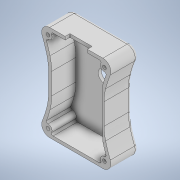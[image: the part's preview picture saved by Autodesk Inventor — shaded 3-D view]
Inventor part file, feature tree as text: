
AUTODESK INVENTOR PART (.ipt)
format: ipt  version: 2021 (Build 250183000, 183)  size: 397,824 bytes
history: native  units: mm
features: extrude x8, sketch x8, mirror x6, fillet x6, shell x2, projected_geometry x2
ambient origin geometry x8: Origin, YZ Plane, XZ Plane, XY Plane, X Axis, Y Axis, Z Axis, Center Point
bodies: Solid1 (feature_tree)
feature tree (32):
  extrude  "Extrusion1"  Depth=17.25mm
  shell  "Shell1"  Thickness=17.25mm
  extrude  "Extrusion2"  Depth=2.0mm
  mirror  "Mirror1"
  mirror  "Mirror2"
  fillet  "Fillet2"  Radius=20.0mm
  fillet  "Fillet3"  Radius=75.0mm
  shell  "Shell2"  Thickness=16.75mm
  extrude  "Extrusion3"  Depth=30.0mm
  mirror  "Mirror3"
  mirror  "Mirror4"
  fillet  "Fillet4"  Radius=5.0mm
  extrude  "Extrusion4"  Depth=2.0mm
  extrude  "Extrusion5"  Depth=5.0mm
  mirror  "Mirror5"
  mirror  "Mirror6"
  fillet  "Fillet5"  Radius=1.0mm
  extrude  "Extrusion6"  Depth=10.0mm
  extrude  "Extrusion8"  Depth=3.75mm
  fillet  "Fillet6"  Radius=8.0mm
  extrude  "Extrusion10"  Depth=0.5mm
  fillet  "Fillet7"  Radius=2.54mm
  sketch  "Sketch1"  dims[d0=35.0mm d1=60.0mm d2=17.25mm d3=0.0mm]
  sketch  "Sketch2"  dims[d4=2.0mm d5=7.0mm d7=20.0mm d8=75.0mm d9=16.75mm d10=0.0mm]
  sketch  "Sketch3"  dims[d12=2.0mm d13=30.0mm d14=5.0mm]
  sketch  "Sketch4"  dims[d15=2.0mm d18=2.5mm]
  sketch  "Sketch5"  dims[d19=5.0mm d20=2.2mm d21=1.0mm]
  sketch  "Sketch6"  dims[d22=10.0mm d23=0.0mm d24=1.0mm]
  sketch  "Sketch8"  dims[d25=0.0mm d26=0.0mm d27=3.75mm d28=8.0mm d29=0.0mm]
  sketch  "Sketch10"  dims[d30=1.0mm d31=8.0mm d33=2.54mm d34=0.0mm d35=0.0mm d37=5.4mm d40=1.1mm d41=10.0mm d42=0.0mm d43=5.0mm d46=14.0mm d47=3.0mm d48=10.0mm d49=0.0mm d50=0.5mm]
  projected_geometry  "Project Cut Edges1"
  projected_geometry  "Project Cut Edges2"
